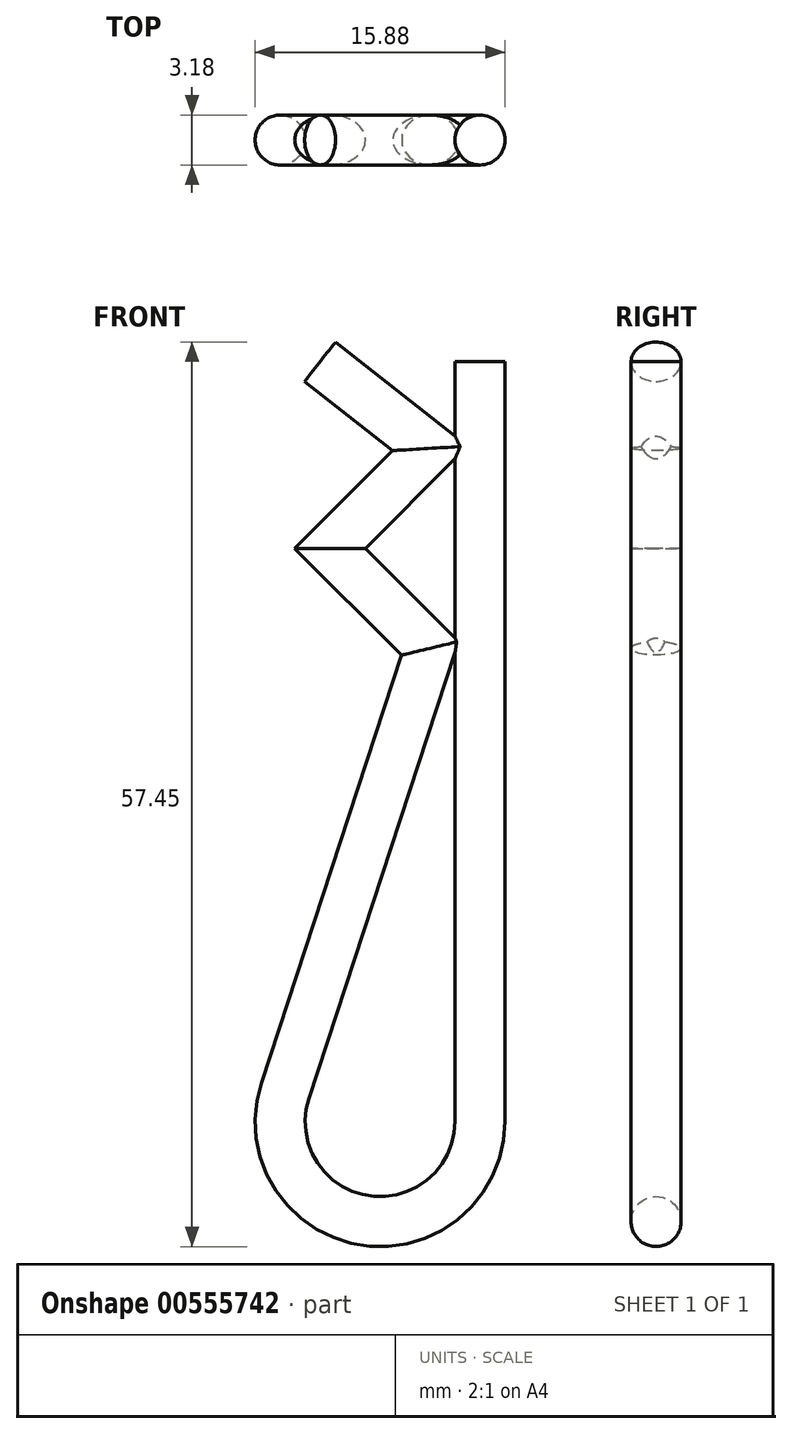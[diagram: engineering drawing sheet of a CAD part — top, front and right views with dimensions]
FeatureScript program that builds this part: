
annotation { "Feature Type Name" : "Feature", "Feature Type Description" : "" }
export const myFeature = defineFeature(function(context is Context, id is Id, definition is map)
    precondition{}
    {
        {
            var Q0;
            Q0=qCreatedBy(makeId("Front.planeOp"),FACE);
            var sketch = newSketch(context, id + "F0", { "sketchPlane" : qUnion([Q0])});
            skLineSegment(sketch, "E0", {"start": v(0, 0) * mm, "end": v(0, -48.26) * mm});
            skCircle(sketch, "E1", {"center": v(-6.35, -48.26) * mm, "radius": 6.35 * mm});
            skLineSegment(sketch, "E2", {"start": v(-12.38, -46.28) * mm, "end": v(-3.17, -18.2) * mm});
            skLineSegment(sketch, "E3", {"start": v(-3.17, -18.2) * mm, "end": v(-9.53, -11.85) * mm});
            skLineSegment(sketch, "E4", {"start": v(-9.53, -11.85) * mm, "end": v(-3.18, -5.5) * mm});
            skLineSegment(sketch, "E5", {"start": v(-3.17, -5.5) * mm, "end": v(-10.16, 0) * mm});
            skArc(sketch, "E6", {"start": v(-12.38, -46.28) * mm, "mid": v(-7.35, -54.53) * mm, "end": v(0, -48.26) * mm});
            skCircle(sketch, "E7", {"center": v(0, -11.85) * mm, "radius": 6.74 * mm});
            skSolve(sketch);
        }
        {
            var Q0;
            Q0=qCreatedBy(makeId("Top.planeOp"),FACE);
            var sketch = newSketch(context, id + "F1", { "sketchPlane" : qUnion([Q0])});
            skCircle(sketch, "E8", {"center": v(0, 0) * mm, "radius": 1.59 * mm});
            skSolve(sketch);
        }
        {
            var Q0;
            Q0=makeQuery(id+"F1.imprint","IMPRINT",FACE,{"disambiguationData":[TD([[makeQuery(id+"F1.imprint","IMPRINT",EDGE,{"derivedFrom":sQuery(id+"F1.wireOp",EDGE,"E8")}),1.0]])]});
            var Q1;
            Q1=sQuery(id+"F0.wireOp",EDGE,"E0");
            var Q2;
            Q2=sQuery(id+"F0.wireOp",EDGE,"E6");
            var Q3;
            Q3=sQuery(id+"F0.wireOp",EDGE,"E2");
            var Q4;
            Q4=sQuery(id+"F0.wireOp",EDGE,"E3");
            var Q5;
            Q5=sQuery(id+"F0.wireOp",EDGE,"E4");
            var Q6;
            Q6=sQuery(id+"F0.wireOp",EDGE,"E5");
            sweep(context, id + "F2", {"profiles" : qUnion([Q0]), "path" : qUnion([Q1, Q2, Q3, Q4, Q5, Q6])});
        }
    });
